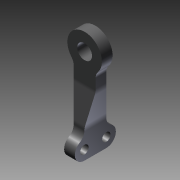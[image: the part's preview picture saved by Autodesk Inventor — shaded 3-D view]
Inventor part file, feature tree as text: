
AUTODESK INVENTOR PART (.ipt)
format: ipt  version: 2011 SP1 (Build 150282100, 282)  size: 162,304 bytes
history: native  units: mm
features: other x42, sketch x5, revolve x3, extrude x2
ambient origin geometry x8: Origin, YZ Plane, XZ Plane, XY Plane, X Axis, Y Axis, Z Axis, Center Point
bodies: Solid1 (feature_tree)
feature tree (52):
  extrude  "Extrusion1"  Depth=40.0mm TaperAngle=0.0deg
  extrude  "Extrusion2"  TaperAngle=360.0deg  [1 undecoded]
  revolve  "Revolution1"  [1 undecoded]
  revolve  "Revolution2"  [1 undecoded]
  revolve  "Revolution3"  [1 undecoded]
  other  "SA1_XY"
  other  "SA1_YZ"
  other  "SA1_ZX"
  other  "SA1_X"
  other  "SA1_Y"
  other  "SA1_Z"
  other  "SA1_Center"
  other  "SA2_XY"
  other  "SA2_YZ"
  other  "SA2_ZX"
  other  "SA2_X"
  other  "SA2_Y"
  other  "SA2_Z"
  other  "SA2_Center"
  other  "SA3_XY"
  other  "SA3_YZ"
  other  "SA3_ZX"
  other  "SA3_X"
  other  "SA3_Y"
  other  "SA3_Z"
  other  "SA3_Center"
  other  "b_left_XY"
  other  "b_left_YZ"
  other  "b_left_ZX"
  other  "b_left_X"
  other  "b_left_Y"
  other  "b_left_Z"
  other  "b_left_Center"
  other  "r_top_XY"
  other  "r_top_YZ"
  other  "r_top_ZX"
  other  "r_top_X"
  other  "r_top_Y"
  other  "r_top_Z"
  other  "r_top_Center"
  other  "z_left_XY"
  other  "z_left_YZ"
  other  "z_left_ZX"
  other  "z_left_X"
  other  "z_left_Y"
  other  "z_left_Z"
  other  "z_left_Center"
  sketch  "Skizze_1"  dims[d0=10.0mm d1=0.0mm d2=40.0mm d3=0.0mm]
  sketch  "Skizze_2"  dims[d4=360.0deg d5=360.0deg]
  sketch  "Skizze_3"  dims[d6=360.0deg]
  sketch  "Skizze_4"
  sketch  "Skizze_5"
note: 4 required parameter values undecoded (feature->parameter linkage not recoverable at this tier; creation-order binding heuristic only, values carry confidence <= 0.55)
